# Revit family: RN 90061 Optifitt-Serra-Wasserzähler-Bogen
name_source: partatom
category: Rohrformteile
units: mm (PartAtom-declared; Revit-internal decimal feet)

## family parameters
Arbeitsebenenbasiert = Nein
Beim Laden mit Abzugskörper schneiden = Nein
Bemaßung runder Anschluss = Durchmesser verwenden
Gemeinsam genutzt = Nein
Immer vertikal = Ja
Teiletyp = Bogen

## types (1)
- DN=50
    1.010.00.2 Blattnummer der Richtlinie = 29
    1.010.00.3 Ausgabedatum (Monat) der Richtlinie = 201308
    1.010.00.4 Herstellername = R. Nussbaum AG
    1.010.00.5 Revisionsdatum der Datei = 20190521
    1.010.00.6 Webadresse des Herstellers = http://www.nussbaum.ch
    1.100.00.4 Produktbezeichnung = Versorgung
    1.110.00.2 Index = 3
    1.110.00.4 Produktbezeichnung = Optifitt-Serra
    1.800.00.3 TGA-Nummer = 01900300000000000000000000000000000000000000000029???000000000000001
    1.800.00.4 Kommentarfeld = 90061.09, Optifitt-Serra-Wasserzähler-Bogen, mit Flansch, DN=50, L=118
    1.810.00.3 Hersteller-Bestellnummer = 90061.09
    1.810.00.4 DATANORM-Nummer = 90061.09
    1.810.00.6 GTIN-Nummer = 7612945690876
    1.960/3L.00.8 Link (URL) = https://www.nussbaum.ch
    29.700.00.4 Produktname = Optifitt-Serra-Wasserzähler-Bogen, mit Flansch
    29.700.00.5 Produktkennung = 2
    29.700.00.6 Querschnittsform = 1
    29.700.00.7 Nennweitensystem = DN
    29.700.00.8 Nenndrucksystem = PN
    29.710.02.10 Formstück-Gewicht [kg] = 4.382
    29.710.02.3 Benennung = Optifitt-Serra-Wasserzähler-Bogen, mit Flansch, DN=50, L=118
    29.710.02.4 Nenndruck = 16
    29.710.02.5 max. zul. Überdruck [hPa] = 1600
    29.710.02.7 max. zul. Dauer-Betriebsdruck [hPa] = 1600
    29.710.02.9 max. zul. Dauer-Betriebstemperatur [°C] = 90
    EnclosingSpace Visibility = Nein
    Hersteller = R. Nussbaum AG
    Modell = 90061.09
    R. Nussbaum AG 90061.09 de Visibility = Ja
    Typenkommentare = Optifitt-Serra-Wasserzähler-Bogen  DN=50
    URL = https://www.nussbaum.ch

## geometry (parser evidence)
native form markers: Sweep x2
no freeform markers — native parametric forms only
